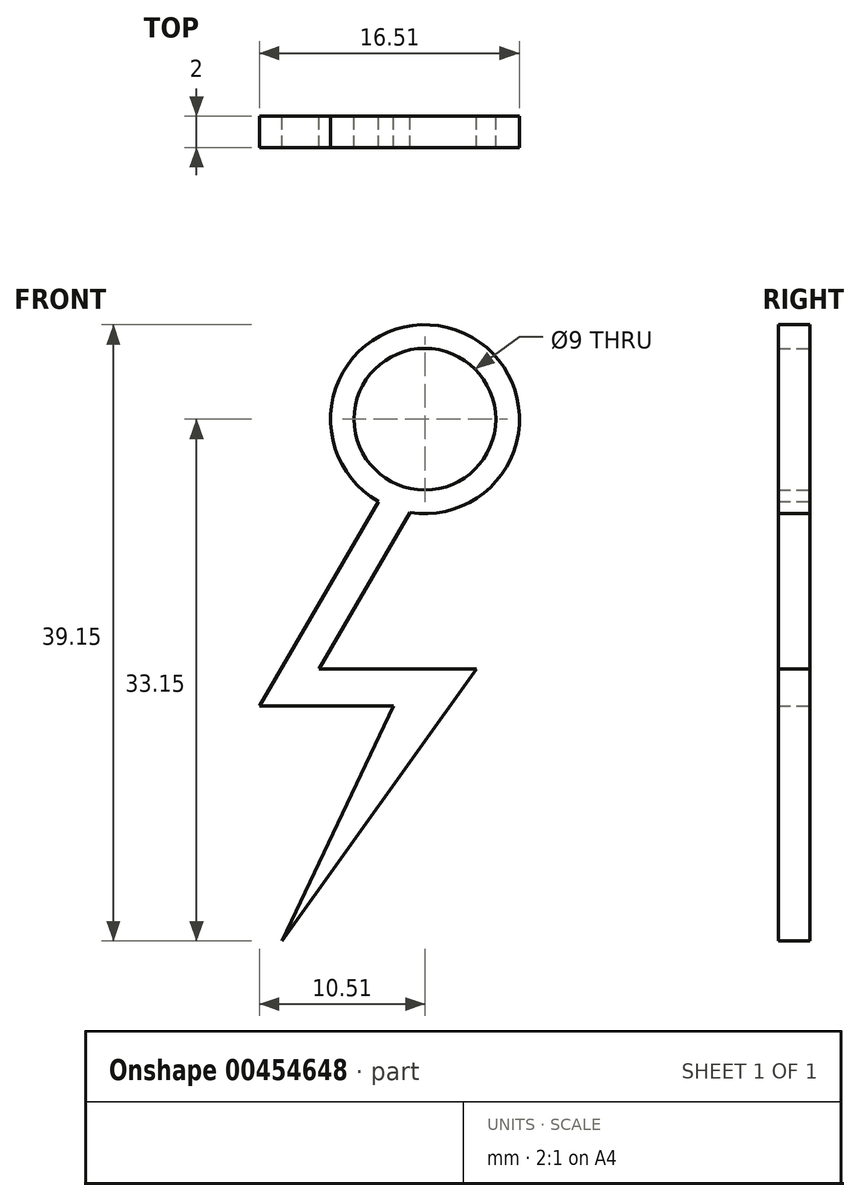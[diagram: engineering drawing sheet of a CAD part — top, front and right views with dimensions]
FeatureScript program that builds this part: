
annotation { "Feature Type Name" : "Feature", "Feature Type Description" : "" }
export const myFeature = defineFeature(function(context is Context, id is Id, definition is map)
    precondition{}
    {
        {
            var Q0;
            Q0=qCreatedBy(makeId("Front.planeOp"),FACE);
            var sketch = newSketch(context, id + "F0", { "sketchPlane" : qUnion([Q0])});
            skCircle(sketch, "E0", {"center": v(0, 0) * mm, "radius": 4.5 * mm});
            skArc(sketch, "E1", {"start": v(-0.95, -5.92) * mm, "mid": v(1.98, 5.66) * mm, "end": v(-2.95, -5.22) * mm});
            skLineSegment(sketch, "E2", {"start": v(-2.95, -5.22) * mm, "end": v(-10.51, -18.21) * mm});
            skLineSegment(sketch, "E3", {"start": v(-10.51, -18.21) * mm, "end": v(-2, -18.21) * mm});
            skLineSegment(sketch, "E4", {"start": v(-2, -18.21) * mm, "end": v(-9.07, -33.15) * mm});
            skLineSegment(sketch, "E5", {"start": v(-9.07, -33.15) * mm, "end": v(3.26, -15.86) * mm});
            skLineSegment(sketch, "E6", {"start": v(3.26, -15.86) * mm, "end": v(-6.73, -15.86) * mm});
            skPoint(sketch, "E6.endSnap0", {"position": v(-6.73, -11.72) * mm});
            skLineSegment(sketch, "E7", {"start": v(-6.73, -15.86) * mm, "end": v(-0.95, -5.92) * mm});
            skPoint(sketch, "E8.trimOffspring.end.orphan", {"position": v(0, -4.29) * mm});
            skSolve(sketch);
        }
        {
            var Q0;
            Q0 = qSketchRegion(id + "F0", true);
            extrude(context, id + "F1", {"entities" : qUnion([Q0]), "depth" : 2 * mm, "offsetDistance" : 25 * mm});
        }
    });
